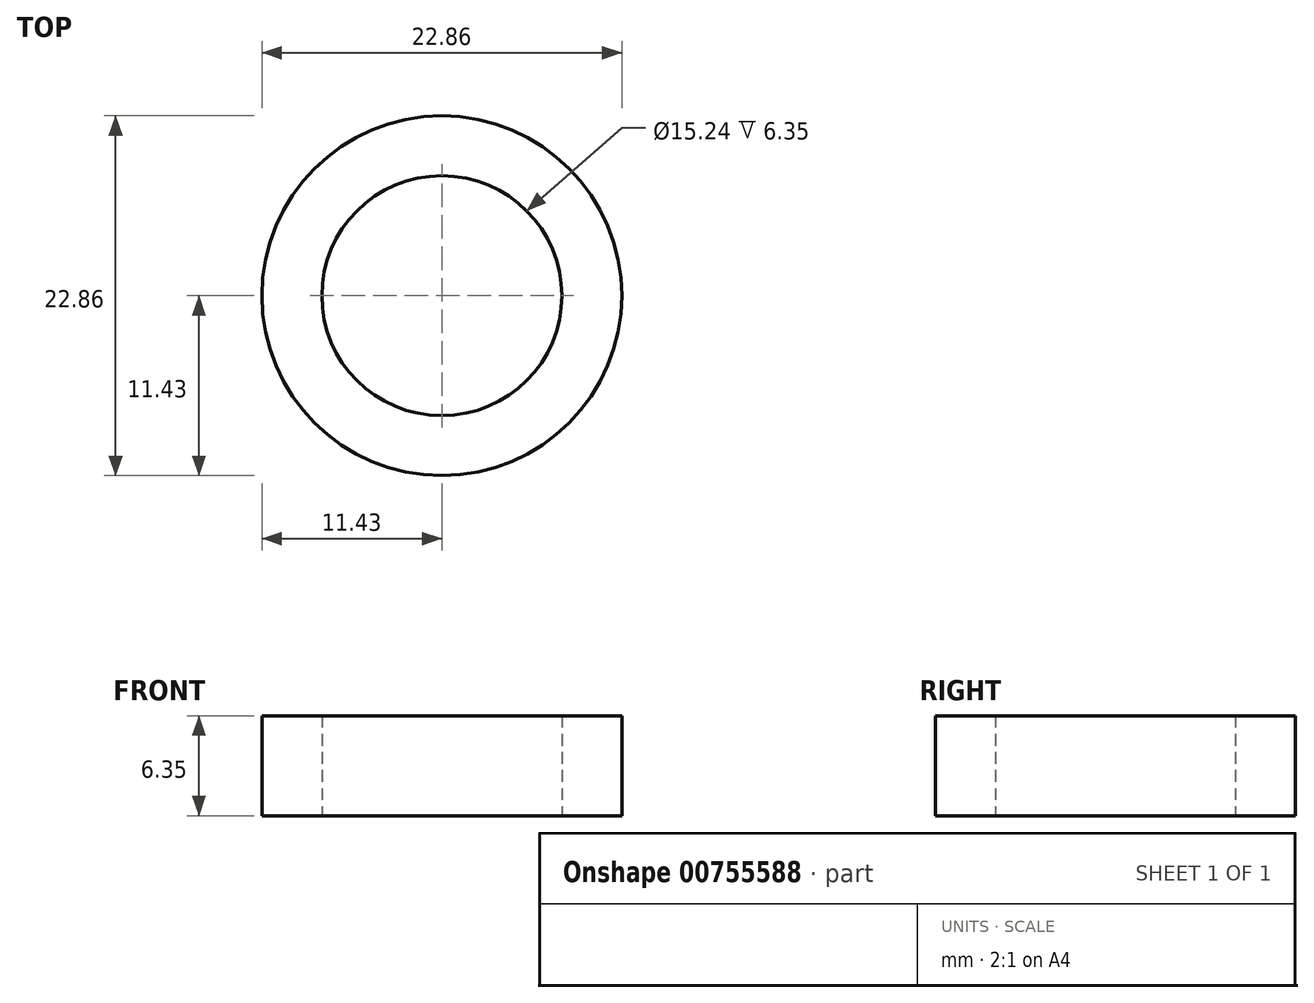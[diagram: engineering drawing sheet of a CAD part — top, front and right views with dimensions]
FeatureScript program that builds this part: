
annotation { "Feature Type Name" : "Feature", "Feature Type Description" : "" }
export const myFeature = defineFeature(function(context is Context, id is Id, definition is map)
    precondition{}
    {
        {
            var Q0;
            Q0=qCreatedBy(makeId("Top.planeOp"),FACE);
            var sketch = newSketch(context, id + "F0", { "sketchPlane" : qUnion([Q0])});
            skCircle(sketch, "E0", {"center": v(0, 0) * mm, "radius": 7.62 * mm});
            skCircle(sketch, "E1", {"center": v(0, 0) * mm, "radius": 11.43 * mm});
            skSolve(sketch);
        }
        {
            var Q0;
            Q0=makeQuery(id+"F0.imprint","IMPRINT",FACE,{"disambiguationData":[TD([[makeQuery(id+"F0.imprint","IMPRINT",EDGE,{"derivedFrom":sQuery(id+"F0.wireOp",EDGE,"E0")}),-1.0]])]});
            extrude(context, id + "F1", {"entities" : qUnion([Q0]), "depth" : 6.35 * mm, "offsetDistance" : 25.4 * mm});
        }
    });
